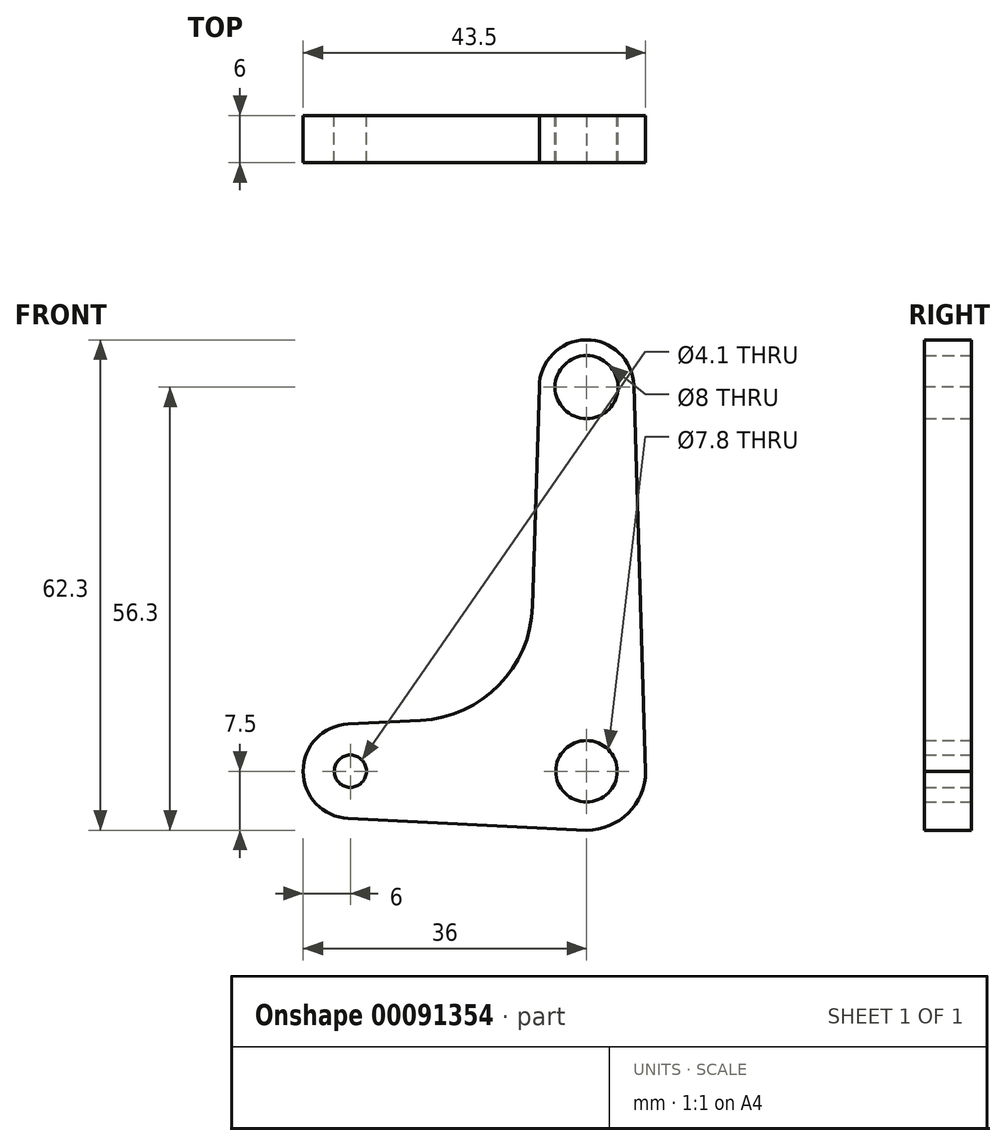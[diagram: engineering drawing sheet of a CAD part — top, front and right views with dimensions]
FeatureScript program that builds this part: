
annotation { "Feature Type Name" : "Feature", "Feature Type Description" : "" }
export const myFeature = defineFeature(function(context is Context, id is Id, definition is map)
    precondition{}
    {
        {
            var Q0;
            Q0=qCreatedBy(makeId("Front.planeOp"),FACE);
            var sketch = newSketch(context, id + "F0", { "sketchPlane" : qUnion([Q0])});
            skLineSegment(sketch, "E0", {"start": v(0, 47.78) * mm, "end": v(0, -11.76) * mm, "construction": true});
            skLineSegment(sketch, "E1", {"start": v(-43.64, 0) * mm, "end": v(12.3, 0) * mm, "construction": true});
            skArc(sketch, "E2", {"start": v(0, 7.5) * mm, "mid": v(-0.19, 7.5) * mm, "end": v(-0.38, 7.5) * mm});
            skArc(sketch, "E3", {"start": v(6, 48.98) * mm, "mid": v(-0.1, 54.8) * mm, "end": v(-6, 48.8) * mm});
            skArc(sketch, "E4", {"start": v(-30.3, 6) * mm, "mid": v(-36, 0) * mm, "end": v(-30.3, -6) * mm});
            skLineSegment(sketch, "E5", {"start": v(7.5, 0) * mm, "end": v(6, 48.98) * mm});
            skLineSegment(sketch, "E6", {"start": v(0, -7.5) * mm, "end": v(-30.3, -6) * mm});
            skLineSegment(sketch, "E7", {"start": v(-6, 48.8) * mm, "end": v(-7.28, 7.14) * mm});
            skLineSegment(sketch, "E8", {"start": v(-30.3, 6) * mm, "end": v(-7.28, 7.14) * mm});
            skArc(sketch, "E9.trimOffspring", {"start": v(-7.5, 0.23) * mm, "mid": v(-7.5, 0.12) * mm, "end": v(-7.5, 0) * mm});
            skLineSegment(sketch, "E10.trimOffspring", {"start": v(-0.37, 7.5) * mm, "end": v(0, 7.5) * mm});
            skLineSegment(sketch, "E11.trimOffspring", {"start": v(-7.5, 0.23) * mm, "end": v(-7.5, 0) * mm});
            skArc(sketch, "E12.trimOffspring", {"start": v(-0.74, -7.46) * mm, "mid": v(5.2, -5.4) * mm, "end": v(7.49, 0.46) * mm});
            skSolve(sketch);
        }
        {
            var Q0;
            {var subQ1=sQuery(id+"F0.wireOp",EDGE,"E3");Q0=makeQuery(id+"F0.imprint","IMPRINT",FACE,{"disambiguationData":[TD([[makeQuery(id+"F0.imprint","IMPRINT",EDGE,{"derivedFrom":subQ1}),1.0]])]});}
            extrude(context, id + "F1", {"entities" : qUnion([Q0]), "oppositeDirection" : true, "depth" : 6 * mm});
        }
        {
            var Q0;
            Q0=makeQuery(id+"F1.opExtrude","CAP_FACE",FACE,{"disambiguationData":[OSD([sQuery(id+"F0.wireOp",EDGE,"E3"),sQuery(id+"F0.wireOp",EDGE,"E4"),sQuery(id+"F0.wireOp",EDGE,"E5"),sQuery(id+"F0.wireOp",EDGE,"E6"),sQuery(id+"F0.wireOp",EDGE,"E7"),sQuery(id+"F0.wireOp",EDGE,"E8"),sQuery(id+"F0.wireOp",EDGE,"E12.trimOffspring")])],"isStart":true});
            var sketch = newSketch(context, id + "F2", { "sketchPlane" : qUnion([Q0])});
            skPoint(sketch, "E13", {"position": v(0, 48.8) * mm});
            skPoint(sketch, "E14", {"position": v(0, 0) * mm});
            skPoint(sketch, "E15", {"position": v(-30, 0) * mm});
            skSolve(sketch);
        }
        {
            var Q0;
            Q0=sQuery(id+"F2.wireOp",VERTEX,"E15");
            var Q1;
            Q1=makeQuery(id+"F1.opExtrude","SWEPT_BODY",BODY,{"disambiguationData":[OSD([sQuery(id+"F0.wireOp",EDGE,"E3"),sQuery(id+"F0.wireOp",EDGE,"E4"),sQuery(id+"F0.wireOp",EDGE,"E5"),sQuery(id+"F0.wireOp",EDGE,"E6"),sQuery(id+"F0.wireOp",EDGE,"E7"),sQuery(id+"F0.wireOp",EDGE,"E8"),sQuery(id+"F0.wireOp",EDGE,"E12.trimOffspring")])]});
            hole(context, id + "F3", {"style" : HoleStyle.SIMPLE, "endStyle" : HoleEndStyle.THROUGH, "standardTappedOrClearance" : lookupTablePath({ "standard" : "ISO", "engagement" : "75%", "pitch" : "0.9 mm", "size" : "M5", "type" : "Tapped" }), "standardBlindInLast" : lookupTablePath({ "standard" : "ISO", "engagement" : "75%", "pitch" : "0.9 mm", "size" : "M5", "type" : "Tapped" }), "holeDiameter" : 4.1 * mm, "locations" : qUnion([Q0]), "scope" : qUnion([Q1]), "isTappedThrough" : true, "showTappedDepth" : true, "startStyle" : HoleStartStyle.SKETCH});
        }
        {
            var Q0;
            Q0=sQuery(id+"F0.wireOp",VERTEX,"E3.center");
            var Q1;
            Q1=makeQuery(id+"F1.opExtrude","SWEPT_BODY",BODY,{"disambiguationData":[OSD([sQuery(id+"F0.wireOp",EDGE,"E3"),sQuery(id+"F0.wireOp",EDGE,"E4"),sQuery(id+"F0.wireOp",EDGE,"E5"),sQuery(id+"F0.wireOp",EDGE,"E6"),sQuery(id+"F0.wireOp",EDGE,"E7"),sQuery(id+"F0.wireOp",EDGE,"E8"),sQuery(id+"F0.wireOp",EDGE,"E12.trimOffspring")])]});
            hole(context, id + "F4", {"style" : HoleStyle.SIMPLE, "endStyle" : HoleEndStyle.THROUGH, "standardTappedOrClearance" : lookupTablePath({ "standard" : "ISO", "size" : "8", "type" : "Drilled" }), "standardBlindInLast" : lookupTablePath({ "standard" : "ISO", "size" : "8", "type" : "Drilled" }), "holeDiameter" : 8 * mm, "locations" : qUnion([Q0]), "scope" : qUnion([Q1]), "isTappedThrough" : true, "startStyle" : HoleStartStyle.SKETCH});
        }
        {
            var Q0;
            Q0=sQuery(id+"F0.wireOp",VERTEX,"E2.center");
            var Q1;
            Q1=makeQuery(id+"F1.opExtrude","SWEPT_BODY",BODY,{"disambiguationData":[OSD([sQuery(id+"F0.wireOp",EDGE,"E3"),sQuery(id+"F0.wireOp",EDGE,"E4"),sQuery(id+"F0.wireOp",EDGE,"E5"),sQuery(id+"F0.wireOp",EDGE,"E6"),sQuery(id+"F0.wireOp",EDGE,"E7"),sQuery(id+"F0.wireOp",EDGE,"E8"),sQuery(id+"F0.wireOp",EDGE,"E12.trimOffspring")])]});
            hole(context, id + "F5", {"style" : HoleStyle.SIMPLE, "endStyle" : HoleEndStyle.THROUGH, "standardTappedOrClearance" : lookupTablePath({ "standard" : "ISO", "size" : "7.8", "type" : "Drilled" }), "standardBlindInLast" : lookupTablePath({ "standard" : "ISO", "size" : "7.8", "type" : "Drilled" }), "holeDiameter" : 7.8 * mm, "locations" : qUnion([Q0]), "scope" : qUnion([Q1]), "isTappedThrough" : true, "startStyle" : HoleStartStyle.SKETCH});
        }
        {
            var Q0;
            Q0=makeQuery(id+"F1.opExtrude","SWEPT_EDGE",EDGE,{"disambiguationData":[OSD([sQuery(id+"F0.wireOp",EDGE,"E7"),sQuery(id+"F0.wireOp",EDGE,"E8")])]});
            fillet(context, id + "F6", {"entities" : qUnion([Q0]), "radius" : 15 * mm, "tangentPropagation" : true, "allowEdgeOverflow" : false});
        }
    });
